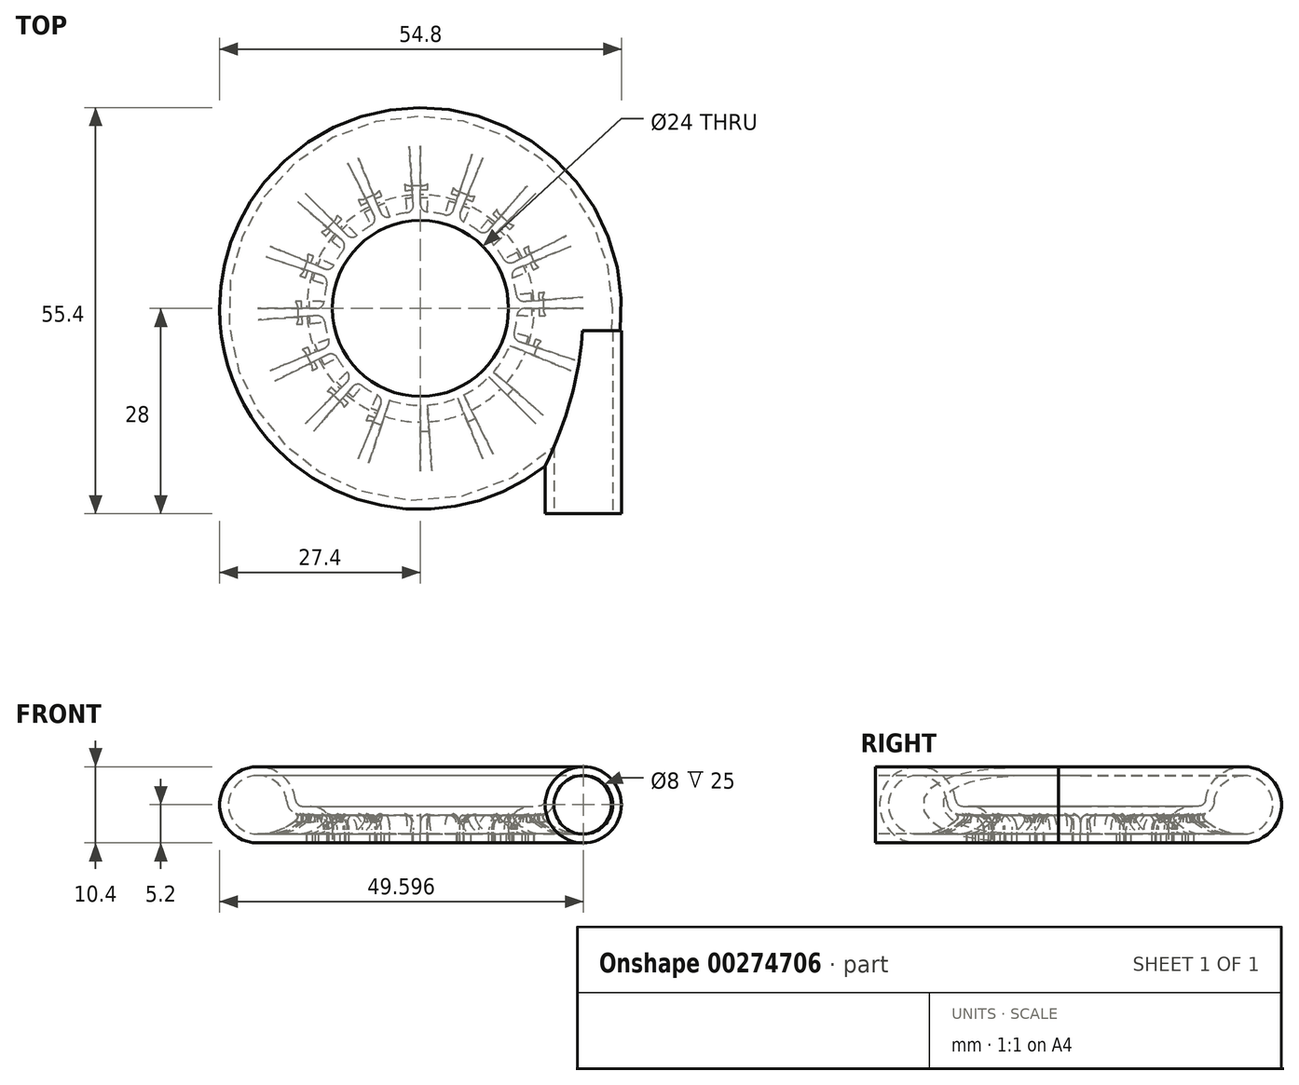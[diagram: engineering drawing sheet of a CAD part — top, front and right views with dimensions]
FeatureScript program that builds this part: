
annotation { "Feature Type Name" : "Feature", "Feature Type Description" : "" }
export const myFeature = defineFeature(function(context is Context, id is Id, definition is map)
    precondition{}
    {
        {
            var Q0;
            Q0=qCreatedBy(makeId("Front.planeOp"),FACE);
            var sketch = newSketch(context, id + "F0", { "sketchPlane" : qUnion([Q0])});
            skLineSegment(sketch, "E0", {"start": v(0, 0) * mm, "end": v(0, 18) * mm, "construction": true});
            skLineSegment(sketch, "E1", {"start": v(12, 0) * mm, "end": v(12, 2) * mm});
            skLineSegment(sketch, "E2", {"start": v(15, 5) * mm, "end": v(16.05, 5) * mm});
            skArc(sketch, "E3", {"start": v(22.2, 0) * mm, "mid": v(26.1, 8.63) * mm, "end": v(17.04, 5.87) * mm});
            skLineSegment(sketch, "E4", {"start": v(22.2, 0) * mm, "end": v(15.5, 0) * mm});
            skLineSegment(sketch, "E5.0", {"start": v(22.2, 1.2) * mm, "end": v(15.5, 1.2) * mm});
            skArc(sketch, "E5.1", {"start": v(22.2, 1.2) * mm, "mid": v(25.16, 7.88) * mm, "end": v(18.22, 5.6) * mm});
            skLineSegment(sketch, "E5.2", {"start": v(15.2, 3.8) * mm, "end": v(16.23, 3.8) * mm});
            skLineSegment(sketch, "E5.3", {"start": v(13.2, 0) * mm, "end": v(13.2, 1.8) * mm});
            skPoint(sketch, "E6.visualSharp", {"position": v(12, 5) * mm});
            skArc(sketch, "E6.filletArc", {"start": v(15, 5) * mm, "mid": v(12.88, 4.12) * mm, "end": v(12, 2) * mm});
            skPoint(sketch, "E7.visualSharp", {"position": v(13.2, 3.8) * mm});
            skArc(sketch, "E7.filletArc", {"start": v(15.2, 3.8) * mm, "mid": v(13.79, 3.21) * mm, "end": v(13.2, 1.8) * mm});
            skLineSegment(sketch, "E8", {"start": v(15.5, 0) * mm, "end": v(15.5, 1.2) * mm});
            skLineSegment(sketch, "E9", {"start": v(12, 0) * mm, "end": v(13.2, 0) * mm});
            skPoint(sketch, "E10.visualSharp", {"position": v(18.45, 3.8) * mm});
            skArc(sketch, "E10.filletArc", {"start": v(16.23, 3.8) * mm, "mid": v(17.57, 4.32) * mm, "end": v(18.22, 5.6) * mm});
            skPoint(sketch, "E11.visualSharp", {"position": v(17, 5) * mm});
            skArc(sketch, "E11.filletArc", {"start": v(16.05, 5) * mm, "mid": v(16.7, 5.25) * mm, "end": v(17.04, 5.87) * mm});
            skLineSegment(sketch, "E12", {"start": v(13.2, 0) * mm, "end": v(15.5, 0) * mm});
            skLineSegment(sketch, "E13.bottom", {"start": v(-10, 4) * mm, "end": v(10, 4) * mm, "construction": true});
            skLineSegment(sketch, "E13.top", {"start": v(-10, 14) * mm, "end": v(10, 14) * mm, "construction": true});
            skLineSegment(sketch, "E13.left", {"start": v(-10, 4) * mm, "end": v(-10, 14) * mm, "construction": true});
            skLineSegment(sketch, "E13.right", {"start": v(10, 4) * mm, "end": v(10, 14) * mm, "construction": true});
            skPoint(sketch, "E13.middle", {"position": v(0, 9) * mm});
            skSolve(sketch);
        }
        {
            var Q0;
            Q0 = qSketchRegion(id + "F0", true);
            var Q1;
            Q1=sQuery(id+"F0.wireOp",EDGE,"E0");
            revolve(context, id + "F1", {"entities" : qUnion([Q0]), "axis" : qUnion([Q1]), "revolveType" : RevolveType.FULL});
        }
        {
            var Q0;
            Q0=qCreatedBy(makeId("Front.planeOp"),FACE);
            var sketch = newSketch(context, id + "F2", { "sketchPlane" : qUnion([Q0])});
            skLineSegment(sketch, "E14.0", {"start": v(13.2, 0) * mm, "end": v(13.2, 1.8) * mm});
            skArc(sketch, "E14.1", {"start": v(15.2, 3.8) * mm, "mid": v(13.79, 3.21) * mm, "end": v(13.2, 1.8) * mm});
            skLineSegment(sketch, "E14.2", {"start": v(15.2, 3.8) * mm, "end": v(16.23, 3.8) * mm});
            skLineSegment(sketch, "E14.3", {"start": v(22.2, 1.2) * mm, "end": v(15.5, 1.2) * mm});
            skLineSegment(sketch, "E14.4", {"start": v(15.5, 0) * mm, "end": v(15.5, 1.2) * mm});
            skLineSegment(sketch, "E15", {"start": v(13.2, 0) * mm, "end": v(15.5, 0) * mm});
            skArc(sketch, "E16", {"start": v(16.23, 3.8) * mm, "mid": v(18.94, 1.88) * mm, "end": v(22.2, 1.2) * mm});
            skSolve(sketch);
        }
        {
            var Q0;
            Q0=qCreatedBy(makeId("Front.planeOp"),FACE);
            cPlane(context, id + "F3", {"entities" : qUnion([Q0]), "cplaneType" : CPlaneType.OFFSET, "offset" : 28 * mm, "width" : 150 * mm, "height" : 150 * mm});
        }
        {
            var Q0;
            Q0=qCreatedBy(id+"F3.planeOp",FACE);
            var sketch = newSketch(context, id + "F4", { "sketchPlane" : qUnion([Q0])});
            skPoint(sketch, "E17.0", {"position": v(22.2, 5.2) * mm});
            skPoint(sketch, "E17.1", {"position": v(26.1, 8.63) * mm});
            skPoint(sketch, "E17.2", {"position": v(25.16, 7.88) * mm});
            skCircle(sketch, "E18", {"center": v(22.2, 5.2) * mm, "radius": 5.2 * mm});
            skSolve(sketch);
        }
        {
            var Q0;
            Q0=makeQuery(id+"F4.imprint","IMPRINT",FACE,{"disambiguationData":[TD([[makeQuery(id+"F4.imprint","IMPRINT",EDGE,{"derivedFrom":sQuery(id+"F4.wireOp",EDGE,"E18")}),1.0]])]});
            extrude(context, id + "F5", {"entities" : qUnion([Q0]), "operationType" : NewBodyOperationType.ADD, "oppositeDirection" : true, "depth" : 25 * mm});
        }
        {
            var Q0;
            Q0=makeQuery(id+"F0.imprint","IMPRINT",FACE,{"disambiguationData":[TD([[makeQuery(id+"F0.imprint","IMPRINT",EDGE,{"derivedFrom":sQuery(id+"F0.wireOp",EDGE,"E5.0")}),-1.0]])]});
            var Q1;
            Q1=sQuery(id+"F0.wireOp",EDGE,"E0");
            revolve(context, id + "F6", {"operationType" : NewBodyOperationType.REMOVE, "entities" : qUnion([Q0]), "axis" : qUnion([Q1]), "revolveType" : RevolveType.FULL, "oppositeDirection" : true});
        }
        {
            var Q0;
            Q0=makeQuery(id+"F5.opExtrude","CAP_FACE",FACE,{"disambiguationData":[OSD([sQuery(id+"F4.wireOp",EDGE,"E18")])],"isStart":true});
            var sketch = newSketch(context, id + "F7", { "sketchPlane" : qUnion([Q0])});
            skPoint(sketch, "E19.0", {"position": v(22.2, 5.2) * mm});
            skPoint(sketch, "E19.1", {"position": v(25.16, 7.88) * mm});
            skCircle(sketch, "E20", {"center": v(22.2, 5.2) * mm, "radius": 4 * mm});
            skSolve(sketch);
        }
        {
            var Q0;
            Q0 = qSketchRegion(id + "F7", true);
            extrude(context, id + "F8", {"entities" : qUnion([Q0]), "operationType" : NewBodyOperationType.REMOVE, "oppositeDirection" : true, "depth" : 25 * mm});
        }
        {
            var Q0;
            Q0 = qSketchRegion(id + "F2", true);
            var Q1;
            Q1=sQuery(id+"F0.wireOp",EDGE,"E0");
            revolve(context, id + "F9", {"entities" : qUnion([Q0]), "axis" : qUnion([Q1]), "revolveType" : RevolveType.ONE_DIRECTION, "angle" : 4 * degree});
        }
        {
            var Q0;
            Q0=makeQuery(id+"F9.opRevolve","SWEPT_BODY",BODY,{"disambiguationData":[OSD([sQuery(id+"F2.wireOp",EDGE,"E14.0"),sQuery(id+"F2.wireOp",EDGE,"E14.1"),sQuery(id+"F2.wireOp",EDGE,"E14.2"),sQuery(id+"F2.wireOp",EDGE,"E14.3"),sQuery(id+"F2.wireOp",EDGE,"E14.4"),sQuery(id+"F2.wireOp",EDGE,"E15"),sQuery(id+"F2.wireOp",EDGE,"E16")])]});
            var Q1;
            Q1=sQuery(id+"F0.wireOp",EDGE,"E0");
            circularPattern(context, id + "F10", {"operationType" : NewBodyOperationType.ADD, "entities" : qUnion([Q0]), "axis" : qUnion([Q1]), "angle" : 360 * degree, "instanceCount" : 16, "equalSpace" : true});
        }
        {
            var Q0;
            Q0=makeQuery(id+"F6.boolean.opBoolean","COPY",FACE,{"derivedFrom":makeQuery(id+"F6.opRevolve","SWEPT_FACE",FACE,{"disambiguationData":[OSD([sQuery(id+"F0.wireOp",EDGE,"E10.filletArc")])]})});
            fillet(context, id + "F11", {"entities" : qUnion([Q0]), "radius" : 0.5 * mm, "tangentPropagation" : true, "allowEdgeOverflow" : false});
        }
        {
            var Q0;
            {var subQ0=sQuery(id+"F2.wireOp",EDGE,"E16");var subQ1=sQuery(id+"F2.wireOp",EDGE,"E15");var subQ2=sQuery(id+"F2.wireOp",EDGE,"E14.4");var subQ3=sQuery(id+"F2.wireOp",EDGE,"E14.3");var subQ4=sQuery(id+"F2.wireOp",EDGE,"E14.2");var subQ5=sQuery(id+"F2.wireOp",EDGE,"E14.1");var subQ6=sQuery(id+"F2.wireOp",EDGE,"E14.0");Q0=makeQuery(id+"F10.boolean.opBoolean","SPLIT",FACE,{"disambiguationData":[TD([makeQuery(id+"F9.opRevolve","CAP_FACE",FACE,{"disambiguationData":[OSD([subQ6,subQ5,subQ4,subQ3,subQ2,subQ1,subQ0])],"isStart":true})])],"derivedFrom":makeQuery(id+"F6.boolean.opBoolean","COPY",FACE,{"derivedFrom":makeQuery(id+"F6.opRevolve","SWEPT_FACE",FACE,{"disambiguationData":[OSD([sQuery(id+"F0.wireOp",EDGE,"E5.2")])]})})});}
            var Q1;
            {var subQ0=sQuery(id+"F2.wireOp",EDGE,"E16");var subQ1=sQuery(id+"F2.wireOp",EDGE,"E15");var subQ2=sQuery(id+"F2.wireOp",EDGE,"E14.4");var subQ3=sQuery(id+"F2.wireOp",EDGE,"E14.3");var subQ4=sQuery(id+"F2.wireOp",EDGE,"E14.2");var subQ5=sQuery(id+"F2.wireOp",EDGE,"E14.1");var subQ6=sQuery(id+"F2.wireOp",EDGE,"E14.0");Q1=makeQuery(id+"F10.boolean.opBoolean","SPLIT",FACE,{"disambiguationData":[TD([makeQuery(id+"F9.opRevolve","CAP_FACE",FACE,{"disambiguationData":[OSD([subQ6,subQ5,subQ4,subQ3,subQ2,subQ1,subQ0])],"isStart":false})])],"derivedFrom":makeQuery(id+"F6.boolean.opBoolean","COPY",FACE,{"derivedFrom":makeQuery(id+"F6.opRevolve","SWEPT_FACE",FACE,{"disambiguationData":[OSD([sQuery(id+"F0.wireOp",EDGE,"E5.2")])]})})});}
            var Q2;
            {var subQ0=sQuery(id+"F2.wireOp",EDGE,"E16");var subQ2=sQuery(id+"F2.wireOp",EDGE,"E15");var subQ3=sQuery(id+"F2.wireOp",EDGE,"E14.4");var subQ4=sQuery(id+"F2.wireOp",EDGE,"E14.3");var subQ5=sQuery(id+"F2.wireOp",EDGE,"E14.2");var subQ6=sQuery(id+"F2.wireOp",EDGE,"E14.1");var subQ7=sQuery(id+"F2.wireOp",EDGE,"E14.0");Q2=makeQuery(id+"F10.boolean.opBoolean","SPLIT",FACE,{"disambiguationData":[TD([makeQuery(id+"F10.opPattern","COPY",FACE,{"derivedFrom":makeQuery(id+"F9.opRevolve","CAP_FACE",FACE,{"disambiguationData":[OSD([subQ7,subQ6,subQ5,subQ4,subQ3,subQ2,subQ0])],"isStart":false}),"instanceName":"1"})])],"derivedFrom":makeQuery(id+"F6.boolean.opBoolean","COPY",FACE,{"derivedFrom":makeQuery(id+"F6.opRevolve","SWEPT_FACE",FACE,{"disambiguationData":[OSD([sQuery(id+"F0.wireOp",EDGE,"E5.2")])]})})});}
            var Q3;
            {var subQ0=sQuery(id+"F2.wireOp",EDGE,"E16");var subQ1=sQuery(id+"F2.wireOp",EDGE,"E15");var subQ2=sQuery(id+"F2.wireOp",EDGE,"E14.4");var subQ3=sQuery(id+"F2.wireOp",EDGE,"E14.3");var subQ4=sQuery(id+"F2.wireOp",EDGE,"E14.2");var subQ5=sQuery(id+"F2.wireOp",EDGE,"E14.1");var subQ6=sQuery(id+"F2.wireOp",EDGE,"E14.0");Q3=makeQuery(id+"F10.boolean.opBoolean","SPLIT",FACE,{"disambiguationData":[TD([makeQuery(id+"F10.opPattern","COPY",FACE,{"derivedFrom":makeQuery(id+"F9.opRevolve","CAP_FACE",FACE,{"disambiguationData":[OSD([subQ6,subQ5,subQ4,subQ3,subQ2,subQ1,subQ0])],"isStart":false}),"instanceName":"2"})])],"derivedFrom":makeQuery(id+"F6.boolean.opBoolean","COPY",FACE,{"derivedFrom":makeQuery(id+"F6.opRevolve","SWEPT_FACE",FACE,{"disambiguationData":[OSD([sQuery(id+"F0.wireOp",EDGE,"E5.2")])]})})});}
            var Q4;
            {var subQ0=sQuery(id+"F2.wireOp",EDGE,"E16");var subQ2=sQuery(id+"F2.wireOp",EDGE,"E15");var subQ3=sQuery(id+"F2.wireOp",EDGE,"E14.4");var subQ4=sQuery(id+"F2.wireOp",EDGE,"E14.3");var subQ5=sQuery(id+"F2.wireOp",EDGE,"E14.2");var subQ6=sQuery(id+"F2.wireOp",EDGE,"E14.1");var subQ7=sQuery(id+"F2.wireOp",EDGE,"E14.0");Q4=makeQuery(id+"F10.boolean.opBoolean","SPLIT",FACE,{"disambiguationData":[TD([makeQuery(id+"F10.opPattern","COPY",FACE,{"derivedFrom":makeQuery(id+"F9.opRevolve","CAP_FACE",FACE,{"disambiguationData":[OSD([subQ7,subQ6,subQ5,subQ4,subQ3,subQ2,subQ0])],"isStart":false}),"instanceName":"3"})])],"derivedFrom":makeQuery(id+"F6.boolean.opBoolean","COPY",FACE,{"derivedFrom":makeQuery(id+"F6.opRevolve","SWEPT_FACE",FACE,{"disambiguationData":[OSD([sQuery(id+"F0.wireOp",EDGE,"E5.2")])]})})});}
            var Q5;
            {var subQ0=sQuery(id+"F2.wireOp",EDGE,"E16");var subQ2=sQuery(id+"F2.wireOp",EDGE,"E15");var subQ3=sQuery(id+"F2.wireOp",EDGE,"E14.4");var subQ4=sQuery(id+"F2.wireOp",EDGE,"E14.3");var subQ5=sQuery(id+"F2.wireOp",EDGE,"E14.2");var subQ6=sQuery(id+"F2.wireOp",EDGE,"E14.1");var subQ7=sQuery(id+"F2.wireOp",EDGE,"E14.0");Q5=makeQuery(id+"F10.boolean.opBoolean","SPLIT",FACE,{"disambiguationData":[TD([makeQuery(id+"F10.opPattern","COPY",FACE,{"derivedFrom":makeQuery(id+"F9.opRevolve","CAP_FACE",FACE,{"disambiguationData":[OSD([subQ7,subQ6,subQ5,subQ4,subQ3,subQ2,subQ0])],"isStart":false}),"instanceName":"4"})])],"derivedFrom":makeQuery(id+"F6.boolean.opBoolean","COPY",FACE,{"derivedFrom":makeQuery(id+"F6.opRevolve","SWEPT_FACE",FACE,{"disambiguationData":[OSD([sQuery(id+"F0.wireOp",EDGE,"E5.2")])]})})});}
            var Q6;
            {var subQ0=sQuery(id+"F2.wireOp",EDGE,"E16");var subQ1=sQuery(id+"F2.wireOp",EDGE,"E15");var subQ2=sQuery(id+"F2.wireOp",EDGE,"E14.4");var subQ3=sQuery(id+"F2.wireOp",EDGE,"E14.3");var subQ4=sQuery(id+"F2.wireOp",EDGE,"E14.2");var subQ5=sQuery(id+"F2.wireOp",EDGE,"E14.1");var subQ6=sQuery(id+"F2.wireOp",EDGE,"E14.0");Q6=makeQuery(id+"F10.boolean.opBoolean","SPLIT",FACE,{"disambiguationData":[TD([makeQuery(id+"F10.opPattern","COPY",FACE,{"derivedFrom":makeQuery(id+"F9.opRevolve","CAP_FACE",FACE,{"disambiguationData":[OSD([subQ6,subQ5,subQ4,subQ3,subQ2,subQ1,subQ0])],"isStart":false}),"instanceName":"5"})])],"derivedFrom":makeQuery(id+"F6.boolean.opBoolean","COPY",FACE,{"derivedFrom":makeQuery(id+"F6.opRevolve","SWEPT_FACE",FACE,{"disambiguationData":[OSD([sQuery(id+"F0.wireOp",EDGE,"E5.2")])]})})});}
            var Q7;
            {var subQ0=sQuery(id+"F2.wireOp",EDGE,"E16");var subQ2=sQuery(id+"F2.wireOp",EDGE,"E15");var subQ3=sQuery(id+"F2.wireOp",EDGE,"E14.4");var subQ4=sQuery(id+"F2.wireOp",EDGE,"E14.3");var subQ5=sQuery(id+"F2.wireOp",EDGE,"E14.2");var subQ6=sQuery(id+"F2.wireOp",EDGE,"E14.1");var subQ7=sQuery(id+"F2.wireOp",EDGE,"E14.0");Q7=makeQuery(id+"F10.boolean.opBoolean","SPLIT",FACE,{"disambiguationData":[TD([makeQuery(id+"F10.opPattern","COPY",FACE,{"derivedFrom":makeQuery(id+"F9.opRevolve","CAP_FACE",FACE,{"disambiguationData":[OSD([subQ7,subQ6,subQ5,subQ4,subQ3,subQ2,subQ0])],"isStart":false}),"instanceName":"6"})])],"derivedFrom":makeQuery(id+"F6.boolean.opBoolean","COPY",FACE,{"derivedFrom":makeQuery(id+"F6.opRevolve","SWEPT_FACE",FACE,{"disambiguationData":[OSD([sQuery(id+"F0.wireOp",EDGE,"E5.2")])]})})});}
            var Q8;
            {var subQ0=sQuery(id+"F2.wireOp",EDGE,"E16");var subQ1=sQuery(id+"F2.wireOp",EDGE,"E15");var subQ2=sQuery(id+"F2.wireOp",EDGE,"E14.4");var subQ3=sQuery(id+"F2.wireOp",EDGE,"E14.3");var subQ4=sQuery(id+"F2.wireOp",EDGE,"E14.2");var subQ5=sQuery(id+"F2.wireOp",EDGE,"E14.1");var subQ6=sQuery(id+"F2.wireOp",EDGE,"E14.0");Q8=makeQuery(id+"F10.boolean.opBoolean","SPLIT",FACE,{"disambiguationData":[TD([makeQuery(id+"F10.opPattern","COPY",FACE,{"derivedFrom":makeQuery(id+"F9.opRevolve","CAP_FACE",FACE,{"disambiguationData":[OSD([subQ6,subQ5,subQ4,subQ3,subQ2,subQ1,subQ0])],"isStart":false}),"instanceName":"7"})])],"derivedFrom":makeQuery(id+"F6.boolean.opBoolean","COPY",FACE,{"derivedFrom":makeQuery(id+"F6.opRevolve","SWEPT_FACE",FACE,{"disambiguationData":[OSD([sQuery(id+"F0.wireOp",EDGE,"E5.2")])]})})});}
            var Q9;
            {var subQ0=sQuery(id+"F2.wireOp",EDGE,"E16");var subQ2=sQuery(id+"F2.wireOp",EDGE,"E15");var subQ3=sQuery(id+"F2.wireOp",EDGE,"E14.4");var subQ4=sQuery(id+"F2.wireOp",EDGE,"E14.3");var subQ5=sQuery(id+"F2.wireOp",EDGE,"E14.2");var subQ6=sQuery(id+"F2.wireOp",EDGE,"E14.1");var subQ7=sQuery(id+"F2.wireOp",EDGE,"E14.0");Q9=makeQuery(id+"F10.boolean.opBoolean","SPLIT",FACE,{"disambiguationData":[TD([makeQuery(id+"F10.opPattern","COPY",FACE,{"derivedFrom":makeQuery(id+"F9.opRevolve","CAP_FACE",FACE,{"disambiguationData":[OSD([subQ7,subQ6,subQ5,subQ4,subQ3,subQ2,subQ0])],"isStart":false}),"instanceName":"8"})])],"derivedFrom":makeQuery(id+"F6.boolean.opBoolean","COPY",FACE,{"derivedFrom":makeQuery(id+"F6.opRevolve","SWEPT_FACE",FACE,{"disambiguationData":[OSD([sQuery(id+"F0.wireOp",EDGE,"E5.2")])]})})});}
            var Q10;
            {var subQ0=sQuery(id+"F2.wireOp",EDGE,"E16");var subQ2=sQuery(id+"F2.wireOp",EDGE,"E15");var subQ3=sQuery(id+"F2.wireOp",EDGE,"E14.4");var subQ4=sQuery(id+"F2.wireOp",EDGE,"E14.3");var subQ5=sQuery(id+"F2.wireOp",EDGE,"E14.2");var subQ6=sQuery(id+"F2.wireOp",EDGE,"E14.1");var subQ7=sQuery(id+"F2.wireOp",EDGE,"E14.0");Q10=makeQuery(id+"F10.boolean.opBoolean","SPLIT",FACE,{"disambiguationData":[TD([makeQuery(id+"F10.opPattern","COPY",FACE,{"derivedFrom":makeQuery(id+"F9.opRevolve","CAP_FACE",FACE,{"disambiguationData":[OSD([subQ7,subQ6,subQ5,subQ4,subQ3,subQ2,subQ0])],"isStart":false}),"instanceName":"9"})])],"derivedFrom":makeQuery(id+"F6.boolean.opBoolean","COPY",FACE,{"derivedFrom":makeQuery(id+"F6.opRevolve","SWEPT_FACE",FACE,{"disambiguationData":[OSD([sQuery(id+"F0.wireOp",EDGE,"E5.2")])]})})});}
            var Q11;
            {var subQ0=sQuery(id+"F2.wireOp",EDGE,"E16");var subQ1=sQuery(id+"F2.wireOp",EDGE,"E15");var subQ2=sQuery(id+"F2.wireOp",EDGE,"E14.4");var subQ3=sQuery(id+"F2.wireOp",EDGE,"E14.3");var subQ4=sQuery(id+"F2.wireOp",EDGE,"E14.2");var subQ5=sQuery(id+"F2.wireOp",EDGE,"E14.1");var subQ6=sQuery(id+"F2.wireOp",EDGE,"E14.0");Q11=makeQuery(id+"F10.boolean.opBoolean","SPLIT",FACE,{"disambiguationData":[TD([makeQuery(id+"F10.opPattern","COPY",FACE,{"derivedFrom":makeQuery(id+"F9.opRevolve","CAP_FACE",FACE,{"disambiguationData":[OSD([subQ6,subQ5,subQ4,subQ3,subQ2,subQ1,subQ0])],"isStart":false}),"instanceName":"10"})])],"derivedFrom":makeQuery(id+"F6.boolean.opBoolean","COPY",FACE,{"derivedFrom":makeQuery(id+"F6.opRevolve","SWEPT_FACE",FACE,{"disambiguationData":[OSD([sQuery(id+"F0.wireOp",EDGE,"E5.2")])]})})});}
            fillet(context, id + "F12", {"entities" : qUnion([Q0, Q1, Q2, Q3, Q4, Q5, Q6, Q7, Q8, Q9, Q10, Q11]), "radius" : 1 * mm, "tangentPropagation" : true, "allowEdgeOverflow" : false});
        }
    });
